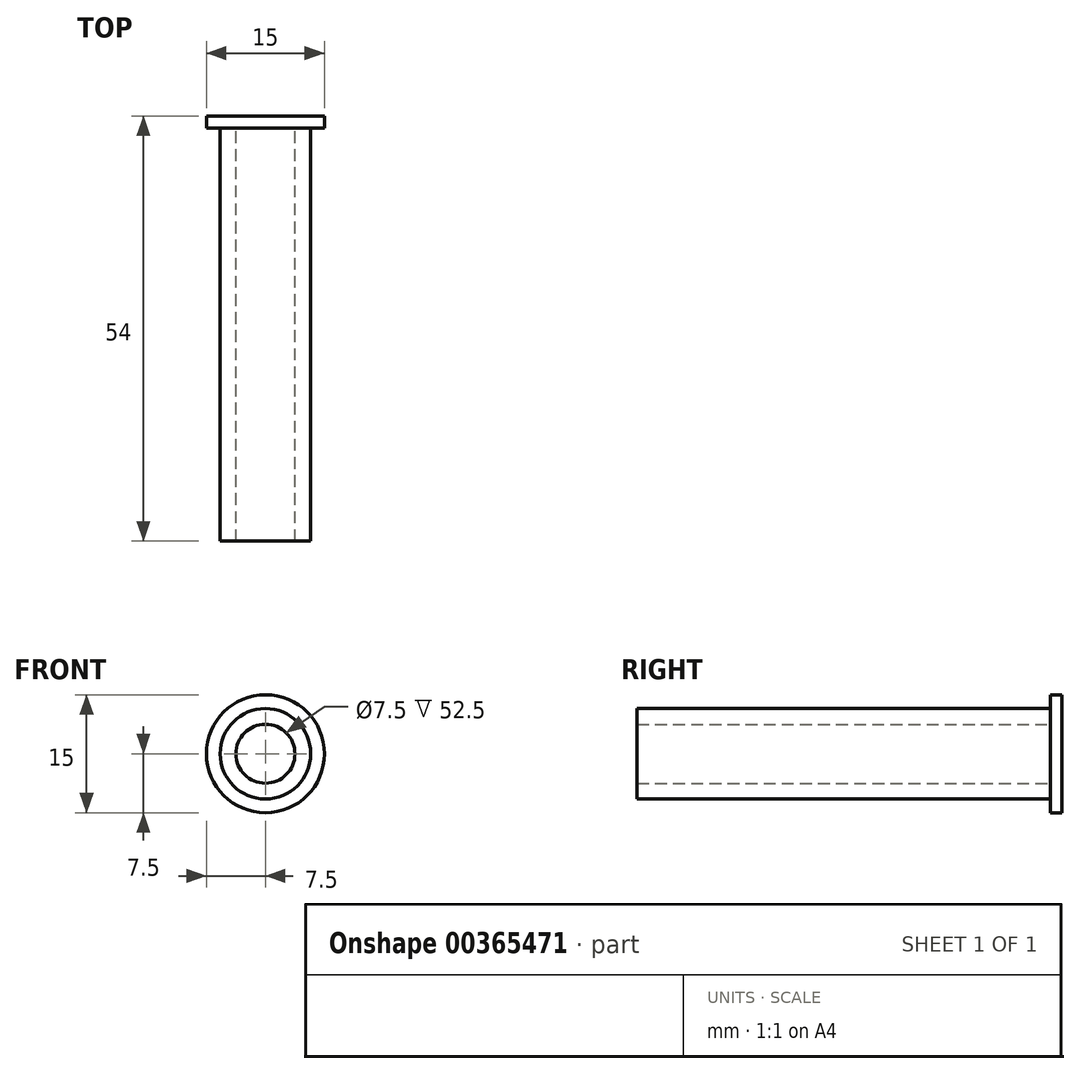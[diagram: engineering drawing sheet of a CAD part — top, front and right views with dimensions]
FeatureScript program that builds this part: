
annotation { "Feature Type Name" : "Feature", "Feature Type Description" : "" }
export const myFeature = defineFeature(function(context is Context, id is Id, definition is map)
    precondition{}
    {
        {
            var Q0;
            Q0=qCreatedBy(makeId("Front.planeOp"),FACE);
            var sketch = newSketch(context, id + "F0", { "sketchPlane" : qUnion([Q0])});
            skCircle(sketch, "E0", {"center": v(0, 0) * mm, "radius": 7.5 * mm});
            skSolve(sketch);
        }
        {
            var Q0;
            Q0 = qSketchRegion(id + "F0", true);
            extrude(context, id + "F1", {"entities" : qUnion([Q0]), "depth" : 1.5 * mm});
        }
        {
            var Q0;
            Q0=makeQuery(id+"F1.opExtrude","CAP_FACE",FACE,{"disambiguationData":[OSD([sQuery(id+"F0.wireOp",EDGE,"E0")])],"isStart":false});
            var sketch = newSketch(context, id + "F2", { "sketchPlane" : qUnion([Q0])});
            skCircle(sketch, "E1", {"center": v(0, 0) * mm, "radius": 5.75 * mm});
            skCircle(sketch, "E2", {"center": v(0, 0) * mm, "radius": 3.75 * mm});
            skSolve(sketch);
        }
        {
            var Q0;
            Q0 = qSketchRegion(id + "F2", true);
            extrude(context, id + "F3", {"entities" : qUnion([Q0]), "operationType" : NewBodyOperationType.ADD, "depth" : 52.5 * mm});
        }
    });
